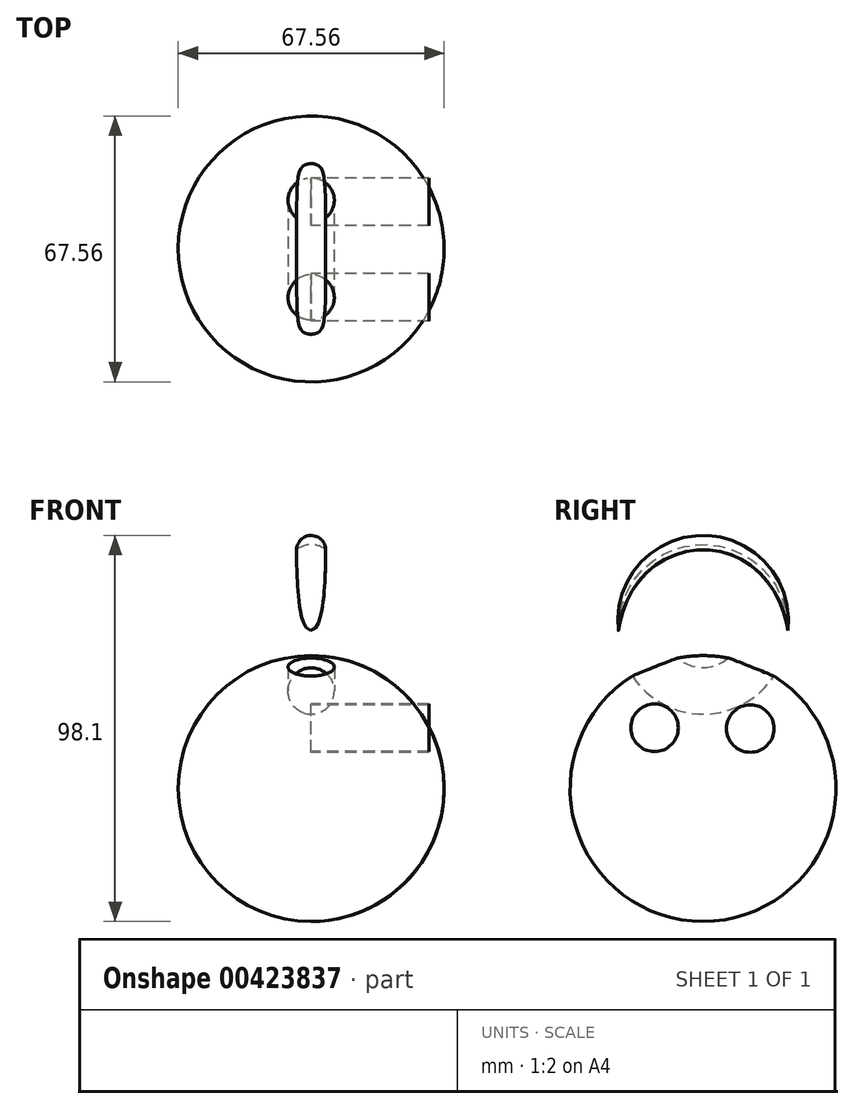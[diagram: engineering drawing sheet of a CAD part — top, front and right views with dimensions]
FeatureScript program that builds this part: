
annotation { "Feature Type Name" : "Feature", "Feature Type Description" : "" }
export const myFeature = defineFeature(function(context is Context, id is Id, definition is map)
    precondition{}
    {
        {
            var Q0;
            Q0=qCreatedBy(makeId("Front.planeOp"),FACE);
            var sketch = newSketch(context, id + "F0", { "sketchPlane" : qUnion([Q0])});
            skArc(sketch, "E0", {"start": v(0, -36.62) * mm, "mid": v(33.78, -2.84) * mm, "end": v(0, 30.94) * mm});
            skLineSegment(sketch, "E1", {"start": v(0, 30.94) * mm, "end": v(0, -36.62) * mm});
            skSolve(sketch);
        }
        {
            var Q0;
            Q0 = qSketchRegion(id + "F0", true);
            var Q1;
            Q1=sQuery(id+"F0.wireOp",EDGE,"E1");
            revolve(context, id + "F1", {"entities" : qUnion([Q0]), "axis" : qUnion([Q1]), "revolveType" : RevolveType.FULL});
        }
        {
            var Q0;
            Q0=qCreatedBy(makeId("Front.planeOp"),FACE);
            var sketch = newSketch(context, id + "F2", { "sketchPlane" : qUnion([Q0])});
            skCircle(sketch, "E2", {"center": v(0, 21.94) * mm, "radius": 5.88 * mm});
            skLineSegment(sketch, "E3", {"start": v(-16.04, 37.6) * mm, "end": v(19.54, 37.6) * mm, "construction": true});
            skSolve(sketch);
        }
        {
            var Q0;
            Q0=qCreatedBy(makeId("Front.planeOp"),FACE);
            var sketch = newSketch(context, id + "F3", { "sketchPlane" : qUnion([Q0])});
            skCircle(sketch, "E4", {"center": v(-0.02, 21.8) * mm, "radius": 3.7 * mm});
            skLineSegment(sketch, "E5", {"start": v(-11.81, 39.79) * mm, "end": v(12.63, 39.79) * mm, "construction": true});
            skSolve(sketch);
        }
        {
            var Q0;
            Q0=makeQuery(id+"F3.imprint","IMPRINT",FACE,{"disambiguationData":[TD([[makeQuery(id+"F3.imprint","IMPRINT",EDGE,{"derivedFrom":sQuery(id+"F3.wireOp",EDGE,"E4")}),1.0]])]});
            var Q1;
            Q1=sQuery(id+"F3.wireOp",EDGE,"E5");
            revolve(context, id + "F4", {"entities" : qUnion([Q0]), "axis" : qUnion([Q1]), "revolveType" : RevolveType.FULL});
        }
        {
            var Q0;
            Q0 = qSketchRegion(id + "F2", true);
            var Q1;
            Q1=sQuery(id+"F2.wireOp",EDGE,"E3");
            var Q2;
            Q2=sQuery(id+"F2.wireOp",EDGE,"E2");
            var Q3;
            Q3=sQuery(id+"F2.wireOp",EDGE,"E3");
            revolve(context, id + "F5", {"operationType" : NewBodyOperationType.REMOVE, "entities" : qUnion([Q0]), "surfaceEntities" : qUnion([Q1, Q2]), "axis" : qUnion([Q3]), "revolveType" : RevolveType.FULL, "oppositeDirection" : true});
        }
        {
            var Q0;
            Q0=qCreatedBy(makeId("Right.planeOp"),FACE);
            var sketch = newSketch(context, id + "F6", { "sketchPlane" : qUnion([Q0])});
            skCircle(sketch, "E6", {"center": v(-12.33, 12.6) * mm, "radius": 6.03 * mm});
            skCircle(sketch, "E7", {"center": v(12, 12.4) * mm, "radius": 6.03 * mm});
            skSolve(sketch);
        }
        {
            var Q0;
            Q0 = qSketchRegion(id + "F6", true);
            extrude(context, id + "F7", {"entities" : qUnion([Q0]), "depth" : 29.97 * mm});
        }
    });
